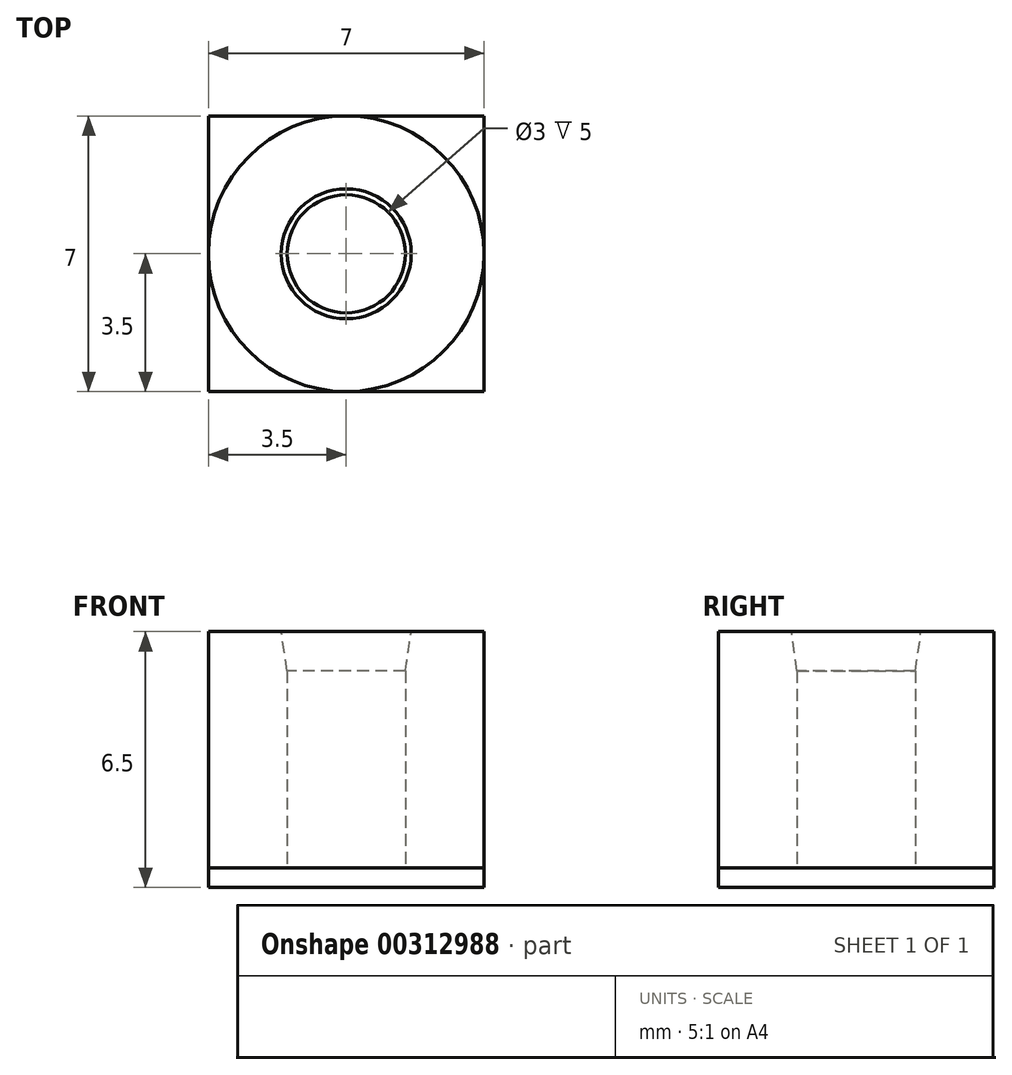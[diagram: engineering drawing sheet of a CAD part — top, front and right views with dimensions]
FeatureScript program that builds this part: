
annotation { "Feature Type Name" : "Feature", "Feature Type Description" : "" }
export const myFeature = defineFeature(function(context is Context, id is Id, definition is map)
    precondition{}
    {
        {
            var Q0;
            Q0=qCreatedBy(makeId("Top.planeOp"),FACE);
            var sketch = newSketch(context, id + "F0", { "sketchPlane" : qUnion([Q0])});
            skLineSegment(sketch, "E0.bottom", {"start": v(0, 0) * mm, "end": v(7, 0) * mm});
            skLineSegment(sketch, "E0.top", {"start": v(0, 7) * mm, "end": v(7, 7) * mm});
            skLineSegment(sketch, "E0.left", {"start": v(0, 0) * mm, "end": v(0, 7) * mm});
            skLineSegment(sketch, "E0.right", {"start": v(7, 0) * mm, "end": v(7, 7) * mm});
            skSolve(sketch);
        }
        {
            var Q0;
            Q0 = qSketchRegion(id + "F0", true);
            extrude(context, id + "F1", {"entities" : qUnion([Q0]), "depth" : .5 * mm});
        }
        {
            var Q0;
            Q0=makeQuery(id+"F1.opExtrude","CAP_FACE",FACE,{"disambiguationData":[OSD([sQuery(id+"F0.wireOp",EDGE,"E0.bottom"),sQuery(id+"F0.wireOp",EDGE,"E0.top"),sQuery(id+"F0.wireOp",EDGE,"E0.left"),sQuery(id+"F0.wireOp",EDGE,"E0.right")])],"isStart":false});
            var sketch = newSketch(context, id + "F2", { "sketchPlane" : qUnion([Q0])});
            skLineSegment(sketch, "E1", {"start": v(3.5, 7) * mm, "end": v(3.5, 0) * mm, "construction": true});
            skCircle(sketch, "E2", {"center": v(3.5, 3.5) * mm, "radius": 3.5 * mm});
            skCircle(sketch, "E3", {"center": v(3.5, 3.5) * mm, "radius": 1.5 * mm});
            skSolve(sketch);
        }
        {
            var Q0;
            Q0 = qSketchRegion(id + "F2", true);
            extrude(context, id + "F3", {"entities" : qUnion([Q0]), "operationType" : NewBodyOperationType.ADD, "depth" : 6 * mm});
        }
        {
            var Q0;
            Q0=makeQuery(id+"F3.opExtrude","CAP_EDGE",EDGE,{"disambiguationData":[OSD([sQuery(id+"F2.wireOp",EDGE,"E3")])],"isStart":false});
            chamfer(context, id + "F4", {"entities" : qUnion([Q0]), "chamferType" : ChamferType.TWO_OFFSETS, "width1" : .15 * mm, "oppositeDirection" : true, "width2" : 1 * mm, "tangentPropagation" : true});
        }
    });
